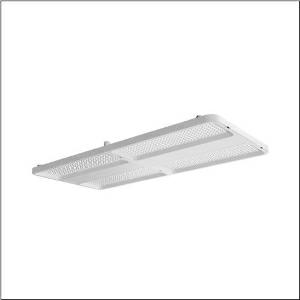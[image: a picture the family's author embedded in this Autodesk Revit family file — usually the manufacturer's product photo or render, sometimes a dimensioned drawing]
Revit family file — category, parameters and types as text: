
# Revit family: highbay_11_maxi_51hn12db4lda
name_source: partatom
category: Lighting Fixtures
units: mm (PartAtom-declared; Revit-internal decimal feet)

## family parameters
Cut with Voids When Loaded = No
Host = Face
Light Source = No
Part Type = Normal
Room Calculation Point = No
Round Connector Dimension = Use Diameter
Shared = No

## types (1)
- --- (1 x LED, 3960 lm, 19.5 W, 4000K)
    Apparent Load = 20 VA
    CIE Flux Codes = 87 98 100 100 100
    Color Rendering = 80
    Color Temperature = 4000K
    Default Elevation = 1800 mm
    Description = high bay luminaire Highbay 11 maxi; direct symmetric wide distribution, light control with lens of PMMA; UGR ≤ 19 (X = 4H | Y = 8H | S = 0.25H | reflection values 70/50/20); luminous flux: 26.000lm; light colour: 840, colour temperature: 4000K, MacAdam ≤ 2 SDCM (initial), colour rendering: CRI > 80; luminous efficacy: 207,3lm/W; rated service life: 100.000h (L95) at AT= 25°C; control: DALI 2; luminaire connection: terminal, 5-pole, max. 2.5mm² (cable entry for one cable, Ø 8.5..16mm); mains connection: 230..240V, AC/DC 0/50..60Hz; connected load: 125,4W; protection rating (complete): IP66; insulation class (complete): insulation class I (protective earthing); protection symbol: D; impact resistance: IK08; certification: CE, ENEC, VDE, UKCA; luminaire for central battery installations according to EN 60598-2-22, internal wiring halogen-free; luminaire Suitable for use in the food industry according to the specifications of IFS-Food, HACCP and/or BRC; LABS conformity tested according to VDMA 24364:2018-05; housing frame of high-performance plastic PA6, matt traffic white (RAL 9016); cover of PMMA; dimension (LxWxH): 946 x 442 x 72mm; permissible operating ambient temperature: -40..+65°C (reducing of maximum allowable ambient temperature of 5°C with ceiling mounting); packaging unit: 1 piece; (delivery without accessories; please order mounting accessories separately)
    Height = 72 mm  [stored 0.23622 ft]
    Lamp = 1 x LED
    Lamp Light Flux = 3960 lm
    Lamp Power = 19.5 W
    Lamp count = 1
    Length = 946 mm
    Luminous efficacy = 203 lm/W
    Manufacturer = Siteco
    ModVariant = No
    Model = 51HN12DB4LDA
    Mounting Place = Ceiling
    Mounting Type = Pendant
    Number of Poles = 1
    OnlyDefault = Yes
    Power Factor = 1
    Product Name = Highbay 11 maxi
    Product group = high bay luminaire
    ProductGroupID = 902
    Protection Class = Protection class I
    Protection Degree = IP 66
    RLX_Detail_Level = 1
    RLX_Emergency_Light_Flux = 0 lm
    RLX_Emergency_Type = 0
    RLX_Emergency_Type_DB = No
    RlxData = <blob elided: 127281 chars, md5=609a1f46>
    Socket = socket
    Standby Power = 0 W
    System Light Flux = 3960 lm
    System Power = 20 W
    Type Comments = : DC mode (central or group accumulator) initial emergency light level
    Type Image = l_1363244.jpg
    URL = http://relux.com
    VarID = @adj_024895
    Voltage = 0 V
    Weight = 0.00 kg
    Width = 442 mm

note: [stored X ft] marks values corroborated as IEEE doubles in the binary element streams (Revit-internal decimal feet)

## geometry (parser evidence)
native form markers: Blend x4, Sweep x11
no freeform markers — native parametric forms only
